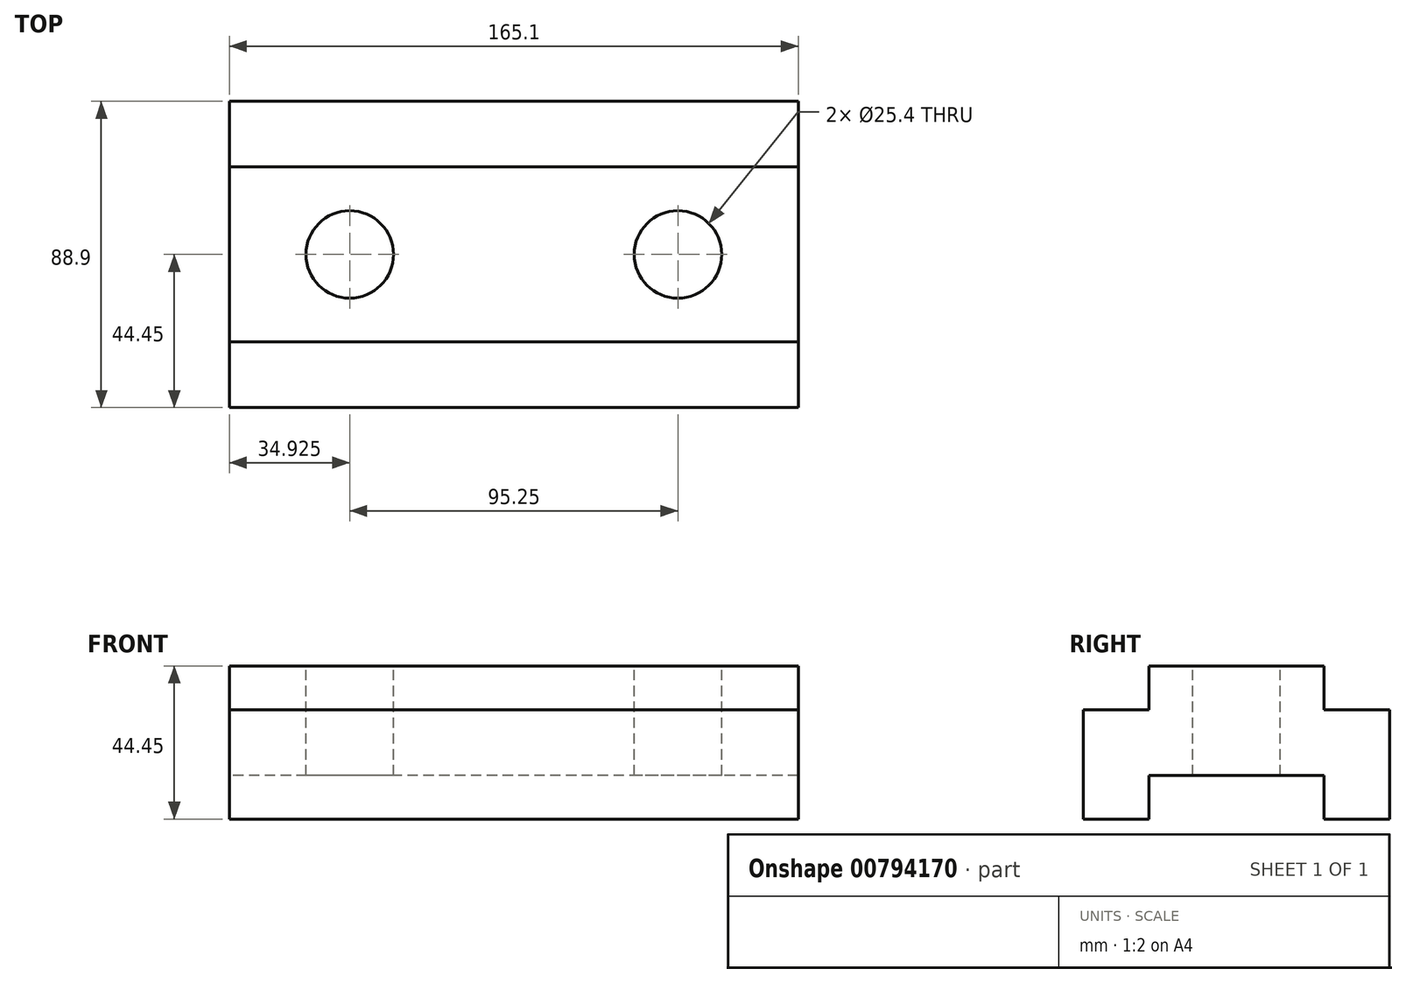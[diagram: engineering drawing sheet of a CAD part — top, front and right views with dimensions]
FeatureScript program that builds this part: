
annotation { "Feature Type Name" : "Feature", "Feature Type Description" : "" }
export const myFeature = defineFeature(function(context is Context, id is Id, definition is map)
    precondition{}
    {
        {
            var Q0;
            Q0=qCreatedBy(makeId("Right.planeOp"),FACE);
            var sketch = newSketch(context, id + "F0", { "sketchPlane" : qUnion([Q0])});
            skLineSegment(sketch, "E0", {"start": v(0, 0) * mm, "end": v(19.05, 0) * mm});
            skLineSegment(sketch, "E1", {"start": v(19.05, 0) * mm, "end": v(19.05, 12.7) * mm});
            skLineSegment(sketch, "E2", {"start": v(19.05, 12.7) * mm, "end": v(69.85, 12.7) * mm});
            skLineSegment(sketch, "E3", {"start": v(69.85, 12.7) * mm, "end": v(69.85, 0) * mm});
            skLineSegment(sketch, "E4", {"start": v(69.85, 0) * mm, "end": v(88.9, 0) * mm});
            skLineSegment(sketch, "E5", {"start": v(88.9, 0) * mm, "end": v(88.9, 31.75) * mm});
            skLineSegment(sketch, "E6", {"start": v(88.9, 31.75) * mm, "end": v(69.85, 31.75) * mm});
            skLineSegment(sketch, "E7", {"start": v(69.85, 31.75) * mm, "end": v(69.85, 44.45) * mm});
            skLineSegment(sketch, "E8", {"start": v(69.85, 44.45) * mm, "end": v(19.05, 44.45) * mm});
            skLineSegment(sketch, "E9", {"start": v(19.05, 44.45) * mm, "end": v(19.05, 31.75) * mm});
            skLineSegment(sketch, "E10", {"start": v(19.05, 31.75) * mm, "end": v(0, 31.75) * mm});
            skLineSegment(sketch, "E11", {"start": v(0.1, 19.05) * mm, "end": v(0, 0) * mm});
            skLineSegment(sketch, "E12", {"start": v(0, 31.75) * mm, "end": v(0, 0) * mm});
            skSolve(sketch);
        }
        {
            var Q0;
            Q0 = qSketchRegion(id + "F0", true);
            extrude(context, id + "F1", {"entities" : qUnion([Q0]), "depth" : 165.1 * mm, "offsetDistance" : 25.4 * mm});
        }
        {
            var Q0;
            Q0=makeQuery(id+"F1.opExtrude","SWEPT_FACE",FACE,{"disambiguationData":[OSD([sQuery(id+"F0.wireOp",EDGE,"E8")])]});
            var sketch = newSketch(context, id + "F2", { "sketchPlane" : qUnion([Q0])});
            skLineSegment(sketch, "E13", {"start": v(0, 44.45) * mm, "end": v(34.93, 44.45) * mm, "construction": true});
            skLineSegment(sketch, "E14", {"start": v(34.93, 44.45) * mm, "end": v(130.18, 44.45) * mm, "construction": true});
            skCircle(sketch, "E15", {"center": v(34.93, 44.45) * mm, "radius": 12.7 * mm});
            skCircle(sketch, "E16", {"center": v(130.18, 44.45) * mm, "radius": 12.7 * mm});
            skSolve(sketch);
        }
        {
            var Q0;
            Q0 = qSketchRegion(id + "F2", true);
            extrude(context, id + "F3", {"entities" : qUnion([Q0]), "operationType" : NewBodyOperationType.REMOVE, "endBound" : BoundingType.UP_TO_NEXT, "oppositeDirection" : true, "depth" : 25.4 * mm, "offsetDistance" : 25.4 * mm});
        }
    });
